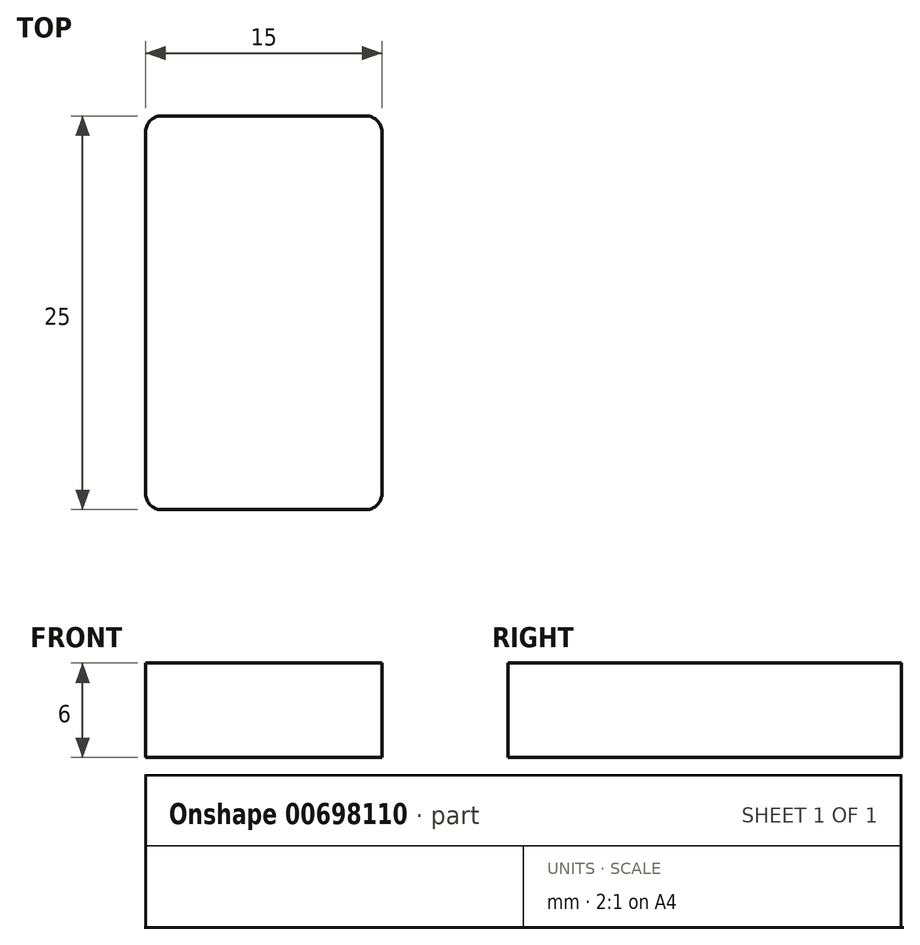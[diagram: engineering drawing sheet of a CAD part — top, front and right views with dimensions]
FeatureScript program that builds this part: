
annotation { "Feature Type Name" : "Feature", "Feature Type Description" : "" }
export const myFeature = defineFeature(function(context is Context, id is Id, definition is map)
    precondition{}
    {
        {
            var Q0;
            Q0=qCreatedBy(makeId("Top.planeOp"),FACE);
            var sketch = newSketch(context, id + "F0", { "sketchPlane" : qUnion([Q0])});
            skLineSegment(sketch, "E0.bottom", {"start": v(6.5, -12.5) * mm, "end": v(-6.5, -12.5) * mm});
            skLineSegment(sketch, "E0.top", {"start": v(6.5, 12.5) * mm, "end": v(-6.5, 12.5) * mm});
            skLineSegment(sketch, "E0.left", {"start": v(7.5, -11.5) * mm, "end": v(7.5, 11.5) * mm});
            skLineSegment(sketch, "E0.right", {"start": v(-7.5, -11.5) * mm, "end": v(-7.5, 11.5) * mm});
            skPoint(sketch, "E0.middle", {"position": v(0, 0) * mm});
            skPoint(sketch, "E1.visualSharp", {"position": v(-7.5, 12.5) * mm});
            skArc(sketch, "E1.filletArc", {"start": v(-6.5, 12.5) * mm, "mid": v(-7.2, 12.2) * mm, "end": v(-7.5, 11.5) * mm});
            skPoint(sketch, "E2.visualSharp", {"position": v(7.5, 12.5) * mm});
            skArc(sketch, "E2.filletArc", {"start": v(7.5, 11.5) * mm, "mid": v(7.2, 12.2) * mm, "end": v(6.5, 12.5) * mm});
            skPoint(sketch, "E3.visualSharp", {"position": v(7.5, -12.5) * mm});
            skArc(sketch, "E3.filletArc", {"start": v(6.5, -12.5) * mm, "mid": v(7.2, -12.2) * mm, "end": v(7.5, -11.5) * mm});
            skPoint(sketch, "E4.visualSharp", {"position": v(-7.5, -12.5) * mm});
            skArc(sketch, "E4.filletArc", {"start": v(-7.5, -11.5) * mm, "mid": v(-7.2, -12.2) * mm, "end": v(-6.5, -12.5) * mm});
            skSolve(sketch);
        }
        {
            var Q0;
            Q0=makeQuery(id+"F0.imprint","IMPRINT",FACE,{"disambiguationData":[TD([[makeQuery(id+"F0.imprint","IMPRINT",EDGE,{"derivedFrom":sQuery(id+"F0.wireOp",EDGE,"E0.bottom")}),-1.0]])]});
            extrude(context, id + "F1", {"entities" : qUnion([Q0]), "endBound" : BoundingType.SYMMETRIC, "depth" : 6 * mm, "offsetDistance" : 25 * mm});
        }
    });
